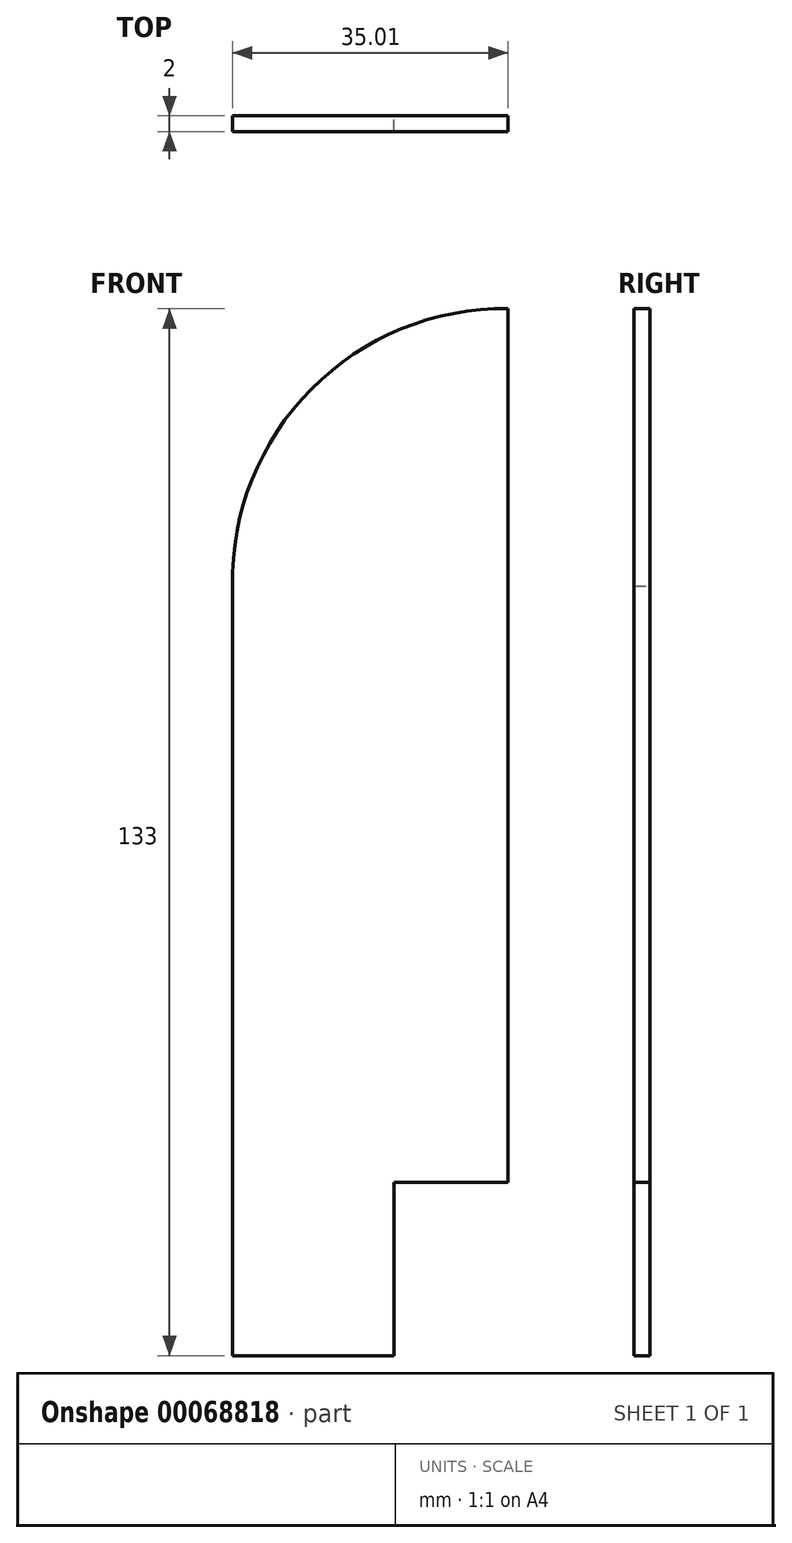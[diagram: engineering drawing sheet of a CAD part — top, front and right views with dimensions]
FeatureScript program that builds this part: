
annotation { "Feature Type Name" : "Feature", "Feature Type Description" : "" }
export const myFeature = defineFeature(function(context is Context, id is Id, definition is map)
    precondition{}
    {
        {
            var Q0;
            Q0=qCreatedBy(makeId("Front.planeOp"),FACE);
            var sketch = newSketch(context, id + "F0", { "sketchPlane" : qUnion([Q0])});
            skLineSegment(sketch, "E0", {"start": v(0, 0) * mm, "end": v(20.5, 0) * mm});
            skLineSegment(sketch, "E1", {"start": v(20.5, 0) * mm, "end": v(20.5, 22) * mm});
            skLineSegment(sketch, "E2", {"start": v(20.5, 22) * mm, "end": v(35, 22) * mm});
            skLineSegment(sketch, "E3", {"start": v(35, 22) * mm, "end": v(35, 133) * mm});
            skLineSegment(sketch, "E4", {"start": v(0, 97.76) * mm, "end": v(0, 0) * mm});
            skArc(sketch, "E5", {"start": v(35, 133) * mm, "mid": v(10.02, 122.8) * mm, "end": v(0, 97.76) * mm});
            skSolve(sketch);
        }
        {
            var Q0;
            Q0 = qSketchRegion(id + "F0", true);
            extrude(context, id + "F1", {"entities" : qUnion([Q0]), "depth" : 2 * mm});
        }
    });
